# Revit family: Haworth_Openest_SprigTable_Round
name_source: partatom
category: Furniture
revit_build: Autodesk Revit 2018 (Build: 20170223_1515(x64)
units: mm (PartAtom-declared; Revit-internal decimal feet)

## family parameters
Always vertical = Yes
Cut with Voids When Loaded = No
OmniClass Number = 23.40.20.00
OmniClass Title = General Furniture and Specialties
Room Calculation Point = No
Shared = No
Work Plane-Based = No

## types (2) — shared parameters
Assembly Code = E2020200
Description = Sprig Table Table
Manufacturer = Haworth
Model = Haworth - Openest Sprig Table - Round
Product Page URL = https://www.haworth.com
Revision No. = 2
Size = Verify Final Dim. w/ Haworth
Sustainability Info = https://www.haworth.com
URL = http://www.haworth.com
Warranty = http://www.haworth.com

## per-type parameters (varying)
| type | 16in Diameter | 24in Diameter | Height | Leg Height | Leg Width | Radius |
| 16in D Table | Yes | No | 1' - 5" | 1' - 4 1/32" | 0' - 6 5/8" | 0' - 8" |
| 24in D Table | No | Yes | 1' - 2" | 1' - 1 1/32" | 0' - 10 9/32" | 1' - 0" |

## geometry (parser evidence)
native form markers: Sweep x7
no freeform markers — native parametric forms only
